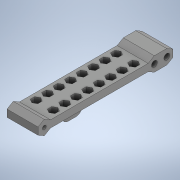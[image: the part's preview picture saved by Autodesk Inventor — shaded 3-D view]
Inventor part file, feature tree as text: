
AUTODESK INVENTOR PART (.ipt)
format: ipt  version: 2020 (Build 240168000, 168)  size: 497,152 bytes
history: native  units: in
note: dims shown in document units (in); Inventor stores cm internally (conversion verified against a paired STEP export)
features: sketch x7, extrude x6, projected_geometry x4, plane x2, mirror x1, fillet x1
ambient origin geometry x8: Origin, YZ Plane, XZ Plane, XY Plane, X Axis, Y Axis, Z Axis, Center Point
bodies: Solid1 (feature_tree)
feature tree (21):
  extrude  "Extrusion1"  Depth=3.4256in
  plane  "Work Plane1"
  extrude  "Extrusion2"  Depth=0.7874in
  sketch  "Sketch4"  dims[d4=0.0in d5=0.0827in]
  extrude  "Extrusion4"  Depth=0.0827in
  plane  "Work Plane2"
  extrude  "Extrusion6"  Depth=3.1106in
  mirror  "Mirror2"
  extrude  "Extrusion7"  Depth=0.315in
  extrude  "Extrusion8"  Depth=0.2362in
  fillet  "Fillet1"  [1 undecoded]
  sketch  "Sketch1"  dims[d0=0.1818in d1=3.4256in]
  sketch  "Sketch2"  dims[d2=0.0984in d3=0.7874in]
  sketch  "Sketch5"  dims[d6=0.7874in d7=0.0in d28=3.1106in]
  sketch  "Sketch7"  dims[d29=0.315in d31=0.315in]
  projected_geometry  "Projected Loop7"
  projected_geometry  "Projected Loop8"
  sketch  "Sketch8"  dims[d33=0.1476in d34=0.2362in d35=0.0in]
  projected_geometry  "Projected Loop9"
  sketch  "Sketch10"  dims[d38=0.315in d39=0.2756in d40=-0.3092in d41=0.0787in d42=0.0787in d43=0.0787in d44=3.1496in d46=0.2913in d47=0.3937in d49=0.3937in d51=3.1496in d53=0.2913in d54=0.3937in d56=0.3937in d58=0.0in d59=0.0in d60=1.0994in d61=0.1378in d63=1.1811in d64=0.1575in d65=0.0in d66=0.126in d67=0.1575in]
  projected_geometry  "Projected Loop10"
note: 1 required parameter value undecoded (feature->parameter linkage not recoverable at this tier; creation-order binding heuristic only, values carry confidence <= 0.55)
